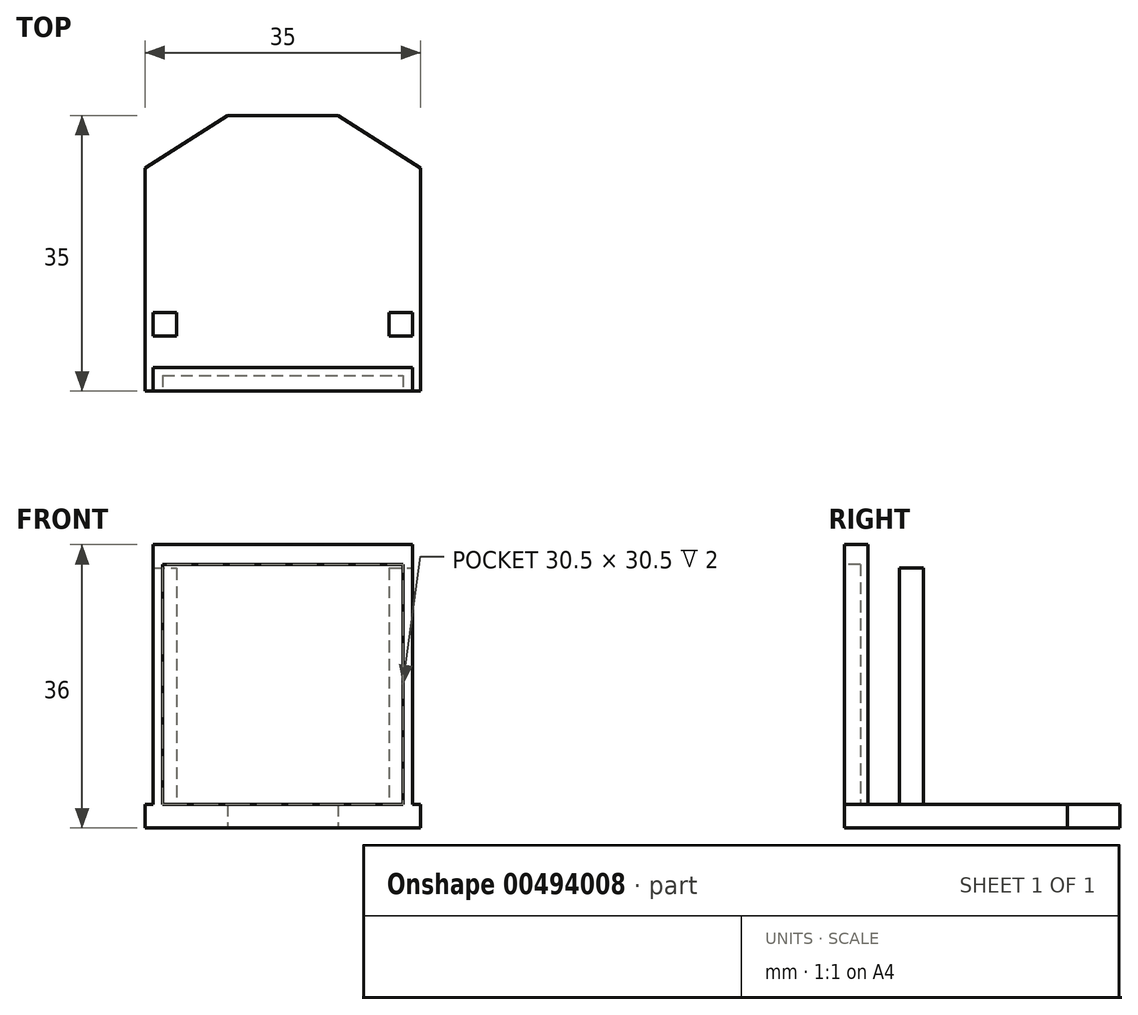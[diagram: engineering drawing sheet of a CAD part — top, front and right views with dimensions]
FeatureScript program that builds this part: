
annotation { "Feature Type Name" : "Feature", "Feature Type Description" : "" }
export const myFeature = defineFeature(function(context is Context, id is Id, definition is map)
    precondition{}
    {
        {
            var Q0;
            Q0=qCreatedBy(makeId("Top.planeOp"),FACE);
            var sketch = newSketch(context, id + "F0", { "sketchPlane" : qUnion([Q0])});
            skLineSegment(sketch, "E0.bottom", {"start": v(7, 17.5) * mm, "end": v(-7, 17.5) * mm});
            skLineSegment(sketch, "E0.top", {"start": v(17.5, -17.5) * mm, "end": v(-17.5, -17.5) * mm});
            skLineSegment(sketch, "E0.left", {"start": v(17.5, 10.82) * mm, "end": v(17.5, -17.5) * mm});
            skLineSegment(sketch, "E0.right", {"start": v(-17.5, 10.82) * mm, "end": v(-17.5, -17.5) * mm});
            skPoint(sketch, "E0.middle", {"position": v(0, 0) * mm});
            skLineSegment(sketch, "E1", {"start": v(-17.5, 10.82) * mm, "end": v(-7, 17.5) * mm});
            skLineSegment(sketch, "E2", {"start": v(17.5, 10.82) * mm, "end": v(7, 17.5) * mm});
            skPoint(sketch, "E3.orphan", {"position": v(-17.5, 17.5) * mm});
            skPoint(sketch, "E4.orphan", {"position": v(17.5, 17.5) * mm});
            skLineSegment(sketch, "E5", {"start": v(17.5, 17.5) * mm, "end": v(7, 17.5) * mm, "construction": true});
            skLineSegment(sketch, "E6", {"start": v(-17.5, 17.5) * mm, "end": v(-7, 17.5) * mm, "construction": true});
            skSolve(sketch);
        }
        {
            var Q0;
            Q0=makeQuery(id+"F0.imprint","IMPRINT",FACE,{"disambiguationData":[TD([[makeQuery(id+"F0.imprint","IMPRINT",EDGE,{"derivedFrom":sQuery(id+"F0.wireOp",EDGE,"E0.bottom")}),1.0]])]});
            extrude(context, id + "F1", {"entities" : qUnion([Q0]), "depth" : 3 * mm});
        }
        {
            var Q0;
            Q0=makeQuery(id+"F1.opExtrude","CAP_FACE",FACE,{"disambiguationData":[OSD([sQuery(id+"F0.wireOp",EDGE,"E0.bottom"),sQuery(id+"F0.wireOp",EDGE,"E0.top"),sQuery(id+"F0.wireOp",EDGE,"E0.left"),sQuery(id+"F0.wireOp",EDGE,"E0.right"),sQuery(id+"F0.wireOp",EDGE,"E1"),sQuery(id+"F0.wireOp",EDGE,"E2")])],"isStart":false});
            var sketch = newSketch(context, id + "F2", { "sketchPlane" : qUnion([Q0])});
            skLineSegment(sketch, "E7.bottom", {"start": v(-16.5, -17.5) * mm, "end": v(16.5, -17.5) * mm});
            skLineSegment(sketch, "E7.top", {"start": v(-16.5, -7.5) * mm, "end": v(16.5, -7.5) * mm});
            skLineSegment(sketch, "E7.left", {"start": v(-16.5, -17.5) * mm, "end": v(-16.5, -7.5) * mm});
            skLineSegment(sketch, "E7.right", {"start": v(16.5, -17.5) * mm, "end": v(16.5, -7.5) * mm});
            skLineSegment(sketch, "E8", {"start": v(-16.5, -10.47) * mm, "end": v(-17.5, -10.47) * mm, "construction": true});
            skLineSegment(sketch, "E9", {"start": v(16.5, -9.81) * mm, "end": v(17.5, -9.81) * mm, "construction": true});
            skLineSegment(sketch, "E10", {"start": v(-16.5, -14.5) * mm, "end": v(16.5, -14.5) * mm});
            skLineSegment(sketch, "E11", {"start": v(13.5, -7.5) * mm, "end": v(13.5, -10.5) * mm});
            skLineSegment(sketch, "E12", {"start": v(13.5, -10.5) * mm, "end": v(16.5, -10.5) * mm});
            skLineSegment(sketch, "E13", {"start": v(-16.5, -10.5) * mm, "end": v(-13.5, -10.5) * mm});
            skLineSegment(sketch, "E14", {"start": v(-13.5, -10.5) * mm, "end": v(-13.5, -7.5) * mm});
            skSolve(sketch);
        }
        {
            var Q0;
            Q0=makeQuery(id+"F2.imprint","IMPRINT",FACE,{"disambiguationData":[TD([[makeQuery(id+"F2.imprint","IMPRINT",EDGE,{"derivedFrom":sQuery(id+"F2.wireOp",EDGE,"56POuJ7X-4QGh-xusb-En4v-FRobhlxDGNVN.bottom")}),1.0]])]});
            var Q1;
            Q1=makeQuery(id+"F2.imprint","IMPRINT",FACE,{"disambiguationData":[TD([[makeQuery(id+"F2.imprint","IMPRINT",EDGE,{"derivedFrom":sQuery(id+"F2.wireOp",EDGE,"Kl537dtf-W63w-vQf8-6AgQ-YYfslVOupGTC.bottom")}),-1.0]])]});
            var Q2;
            {var subQ0=sQuery(id+"F2.wireOp",EDGE,"E7.bottom");Q2=makeQuery(id+"F2.imprint","IMPRINT",FACE,{"disambiguationData":[TD([[makeQuery(id+"F2.imprint","IMPRINT",EDGE,{"derivedFrom":subQ0}),-1.0]])]});}
            var Q3;
            {var subQ4=sQuery(id+"F2.wireOp",EDGE,"E13");Q3=makeQuery(id+"F2.imprint","IMPRINT",FACE,{"disambiguationData":[TD([[makeQuery(id+"F2.imprint","IMPRINT",EDGE,{"derivedFrom":subQ4}),1.0]])]});}
            var Q4;
            {var subQ3=sQuery(id+"F2.wireOp",EDGE,"E11");Q4=makeQuery(id+"F2.imprint","IMPRINT",FACE,{"disambiguationData":[TD([[makeQuery(id+"F2.imprint","IMPRINT",EDGE,{"derivedFrom":subQ3}),1.0]])]});}
            extrude(context, id + "F3", {"entities" : qUnion([Q0, Q1, Q2, Q3, Q4]), "operationType" : NewBodyOperationType.ADD, "depth" : 30 * mm, "offsetDistance" : 25 * mm});
        }
        {
            var Q0;
            Q0=makeQuery(id+"F3.opExtrude","CAP_FACE",FACE,{"disambiguationData":[OSD([sQuery(id+"F2.wireOp",EDGE,"E7.bottom"),sQuery(id+"F2.wireOp",EDGE,"E7.left"),sQuery(id+"F2.wireOp",EDGE,"E7.right"),sQuery(id+"F2.wireOp",EDGE,"E10")])],"isStart":false});
            var sketch = newSketch(context, id + "F4", { "sketchPlane" : qUnion([Q0])});
            skLineSegment(sketch, "E15.0", {"start": v(-16.5, -7.5) * mm, "end": v(16.5, -7.5) * mm});
            skLineSegment(sketch, "E16.0", {"start": v(-16.5, -17.5) * mm, "end": v(-16.5, -7.5) * mm});
            skLineSegment(sketch, "E17.0", {"start": v(16.5, -17.5) * mm, "end": v(16.5, -7.5) * mm});
            skLineSegment(sketch, "E18.bottom", {"start": v(16.5, -7.5) * mm, "end": v(-16.5, -7.5) * mm});
            skLineSegment(sketch, "E18.top", {"start": v(16.5, -17.5) * mm, "end": v(-16.5, -17.5) * mm});
            skLineSegment(sketch, "E18.left", {"start": v(16.5, -7.5) * mm, "end": v(16.5, -17.5) * mm});
            skLineSegment(sketch, "E18.right", {"start": v(-16.5, -7.5) * mm, "end": v(-16.5, -17.5) * mm});
            skSolve(sketch);
        }
        {
            var Q0;
            {var subQ0=sQuery(id+"F4.wireOp",EDGE,"E18.bottom");Q0=makeQuery(id+"F4.imprint","IMPRINT",FACE,{"disambiguationData":[TD([[makeQuery(id+"F4.imprint","IMPRINT",EDGE,{"derivedFrom":subQ0}),1.0]])]});}
            var Q1;
            {var subQ0=sQuery(id+"F4.wireOp",EDGE,"E18.top");Q1=makeQuery(id+"F4.imprint","IMPRINT",FACE,{"disambiguationData":[TD([[makeQuery(id+"F4.imprint","IMPRINT",EDGE,{"derivedFrom":subQ0}),-1.0]])]});}
            extrude(context, id + "F5", {"entities" : qUnion([Q0, Q1]), "operationType" : NewBodyOperationType.ADD, "depth" : 3 * mm});
        }
        {
            var Q0;
            Q0=makeQuery(id+"F5.boolean.opBoolean","MERGE",FACE,{"derivedFrom":[makeQuery(id+"F3.boolean.opBoolean","MERGE",FACE,{"derivedFrom":[makeQuery(id+"F1.opExtrude","SWEPT_FACE",FACE,{"disambiguationData":[OSD([sQuery(id+"F0.wireOp",EDGE,"E0.top")])]}),makeQuery(id+"F3.opExtrude","SWEPT_FACE",FACE,{"disambiguationData":[OSD([sQuery(id+"F2.wireOp",EDGE,"E7.bottom")])]})]}),makeQuery(id+"F5.opExtrude","SWEPT_FACE",FACE,{"disambiguationData":[OSD([sQuery(id+"F4.wireOp",EDGE,"E18.top")])]})]});
            var sketch = newSketch(context, id + "F6", { "sketchPlane" : qUnion([Q0])});
            skLineSegment(sketch, "E19.0", {"start": v(-16.5, 36) * mm, "end": v(-16.5, 3) * mm});
            skLineSegment(sketch, "E20.0", {"start": v(16.5, 36) * mm, "end": v(-16.5, 36) * mm});
            skLineSegment(sketch, "E21.0", {"start": v(16.5, 36) * mm, "end": v(16.5, 3) * mm});
            skLineSegment(sketch, "E22.0", {"start": v(17.5, 3) * mm, "end": v(16.5, 3) * mm});
            skLineSegment(sketch, "E23.0", {"start": v(17.5, 3) * mm, "end": v(17.5, 0) * mm});
            skLineSegment(sketch, "E24.0", {"start": v(17.5, 0) * mm, "end": v(-17.5, 0) * mm});
            skLineSegment(sketch, "E25.0", {"start": v(-17.5, 3) * mm, "end": v(-17.5, 0) * mm});
            skLineSegment(sketch, "E26.0", {"start": v(-16.5, 3) * mm, "end": v(-17.5, 3) * mm});
            skLineSegment(sketch, "E27.bottom", {"start": v(-15.25, 33.5) * mm, "end": v(15.25, 33.5) * mm});
            skLineSegment(sketch, "E27.top", {"start": v(-15.25, 3) * mm, "end": v(15.25, 3) * mm});
            skLineSegment(sketch, "E27.left", {"start": v(-15.25, 33.5) * mm, "end": v(-15.25, 3) * mm});
            skLineSegment(sketch, "E27.right", {"start": v(15.25, 33.5) * mm, "end": v(15.25, 3) * mm});
            skLineSegment(sketch, "E28", {"start": v(15.25, 18.25) * mm, "end": v(16.5, 18.25) * mm, "construction": true});
            skLineSegment(sketch, "E29", {"start": v(-15.25, 18.25) * mm, "end": v(-16.5, 18.25) * mm, "construction": true});
            skSolve(sketch);
        }
        {
            var Q0;
            Q0=makeQuery(id+"F6.imprint","IMPRINT",FACE,{"disambiguationData":[TD([[makeQuery(id+"F6.imprint","IMPRINT",EDGE,{"derivedFrom":sQuery(id+"F6.wireOp",EDGE,"E27.bottom")}),-1.0]])]});
            extrude(context, id + "F7", {"entities" : qUnion([Q0]), "operationType" : NewBodyOperationType.REMOVE, "oppositeDirection" : true, "depth" : 2 * mm});
        }
    });
